# Revit family: QF_BPRO_TAW 10 GN_574240
name_source: partatom
category: Sonderausstattung
revit_build: Autodesk Revit 2018 (Build: 20190510_1515(x64)
units: mm (PartAtom-declared; Revit-internal decimal feet)

## family parameters
Arbeitsebenenbasiert = Nein
Beim Laden mit Abzugskörper schneiden = Nein
Bemaßung runder Anschluss = Durchmesser verwenden
Gemeinsam genutzt = Nein
Immer vertikal = Ja
OmniClass-Nummer = 23.40.40.00
OmniClass-Titel = Food Service Equipment and Furnishings
Raumberechnungspunkt = Nein
Teiletyp = Normal

## types (1)
- TAW 10 GN
    Artikel Nummer = 574240
    Barcode = 0
    Beschreibung = Tablett-Abrümwagen, 1-teilig, beidseitig beschickbar
    Beschreibung durch Hersteller analog Leistungsverzeichniskurztext = Tablett-Abräumwagen, TAW 10 GN


Abmessungen

Länge:				     468 mm
Breite:			     673 mm  
Höhe:			   1550 mm
Höhe inkl. Wagendach (optional):   1586 mm



Ausführung

Der Tablett-Abräumwagen ist einteilig und komplett in CNS 18/10, Werkstoff-Nr. 1.4301 ausgeführt. Die Rahmenkonstruktion besteht aus stabilem Vierkantrohr (25x25 mm und 40x20 mm) und ist komplett verschweißt.
Die Tablettauflagen aus Rundmaterial Ø 6 mm sind als Gestelle ausgeführt, die innerhalb des Rahmens eingehängt und sicher verschraubt sind. Dadurch sind die Auflagegestelle bei Bedarf komplett entnehmbar. Durch die schräg angeschweißten Bügel sind die Tablettauflagen mit integrierter, beidseitiger Durchschubsicherung ausgeführt.
Der Tablett-Abräumwagen kann von beiden Seiten beschickt werden und hat eine Kapazität von 10 Tabletts im GN-Format (530x325 mm). Der Auflagenabstand beträgt 125 mm.
Der Wagen ist fahr¬bar mittels rostfreien Kunststoffrollen gemäß DIN 18867, Teil 8 (4 Lenkrollen, davon 2 mit Feststeller, Rollendurchmesser 125 mm). Runde Wandabweiser aus Kunststoff (Polyamid) an allen vier Ecken schützen vor Beschädigungen.


Zubehör/ Optionen

•	Verkleidung 2-seitig aus Feinblech, doppelseitig elektrolytisch verzinkt, pulverbeschichtet in verschiedenen Farben, zum Einhängen an den Tablett-Abräumwagen. Zur Reinigung einfach und ohne Werkzeug abnehmbar.
•	Verkleidung 2-seitig aus Edelstahl, zum Einhängen an den Tablett-Abräumwagen. Zur Reinigung einfach und ohne Werkzeug abnehmbar.
•	Verkleidung 3-seitig aus Feinblech, doppelseitig elektrolytisch verzinkt, pulverbeschichtet in verschiedenen Farben, zum Einhängen an den Tablett-Abräumwagen. Zur Reinigung einfach und ohne Werkzeug abnehmbar.
•	Verkleidung 3-seitig aus Edelstahl, zum Einhängen an den Tablett-Abräumwagen. Zur Reinigung einfach und ohne Werkzeug abnehmbar.
•	Tür aus Feinblech, zweiwandig für mehr Stabilität, doppelseitig elektrolytisch verzinkt, pulverbeschichtet in verschiedenen Farben. Wahlweise geschlossen oder mit Glaseinsatz aus Einscheiben-Sicherheitsglas (ESG) erhältlich.
•	Tür aus Edelstahl. Wahlweise geschlossen oder mit Glaseinsatz aus Einscheiben-Sicherheitsglas (ESG) erhältlich.
•	Wagendach aus Edelstahl inkl. umlaufender Galerie. Zum Aufsetzen auf den Tablett-Abräumwagen. Zur Reinigung einfach und ohne Werkzeug abnehmbar. Die maximale Flächenlast beträgt 20 kg.
•	Boden aus Edelstahl zum Einlegen in die Rahmenkonstruktion. Zur Reinigung einfach und ohne Werkzeug abnehmbar.
•	Zusätzliche Durchschubsicherung aus Edelstahl
•	Schiebegriff stirnseitig
•	Rollensatz stahlverzinkt


Technische Daten

Werkstoff:		Chromnickelstahl 18/10, Polyamid (PA)	
Gewicht:	ca. 21 kg
Max. Tragfähigkeit Wagen:	150 kg
Max. Tragfähigkeit/ 
Auflagenpaar:	4,5 kg
Anzahl der Auflagenpaare:	10
Kapazität:	 		10 Gastronorm-Tabletts, 		530x325 mm
Auflagenabstand:	125 mm
	

Besonderheit

•	Tablettauflagen mit integrierter, beidseitiger Durchschubsicherung
•	Tablettauflagegestelle komplett entnehmbar
•	Optionale Verkleidung (2-, oder 3-seitig) zum Einhängen an den TAW. Dadurch zur Reinigung einfach abnehmbar.
•	Anbauteile wie Verkleidung, Türen, Dach und Boden jederzeit nachrüstbar.



Fabrikat

Hersteller:			B.PRO
Modell:	TAW 10 GN
Best.Nr.	574 240
    Beschreibung durch Hersteller analog Leistungsverzeichnislangtext = Tablett-Abräumwagen, TAW 10 GN


Abmessungen

Länge:				     468 mm
Breite:			     673 mm  
Höhe:			   1550 mm
Höhe inkl. Wagendach (optional):   1586 mm



Ausführung

Der Tablett-Abräumwagen ist einteilig und komplett in CNS 18/10, Werkstoff-Nr. 1.4301 ausgeführt. Die Rahmenkonstruktion besteht aus stabilem Vierkantrohr (25x25 mm und 40x20 mm) und ist komplett verschweißt.
Die Tablettauflagen aus Rundmaterial Ø 6 mm sind als Gestelle ausgeführt, die innerhalb des Rahmens eingehängt und sicher verschraubt sind. Dadurch sind die Auflagegestelle bei Bedarf komplett entnehmbar. Durch die schräg angeschweißten Bügel sind die Tablettauflagen mit integrierter, beidseitiger Durchschubsicherung ausgeführt.
Der Tablett-Abräumwagen kann von beiden Seiten beschickt werden und hat eine Kapazität von 10 Tabletts im GN-Format (530x325 mm). Der Auflagenabstand beträgt 125 mm.
Der Wagen ist fahr¬bar mittels rostfreien Kunststoffrollen gemäß DIN 18867, Teil 8 (4 Lenkrollen, davon 2 mit Feststeller, Rollendurchmesser 125 mm). Runde Wandabweiser aus Kunststoff (Polyamid) an allen vier Ecken schützen vor Beschädigungen.


Zubehör/ Optionen

•	Verkleidung 2-seitig aus Feinblech, doppelseitig elektrolytisch verzinkt, pulverbeschichtet in verschiedenen Farben, zum Einhängen an den Tablett-Abräumwagen. Zur Reinigung einfach und ohne Werkzeug abnehmbar.
•	Verkleidung 2-seitig aus Edelstahl, zum Einhängen an den Tablett-Abräumwagen. Zur Reinigung einfach und ohne Werkzeug abnehmbar.
•	Verkleidung 3-seitig aus Feinblech, doppelseitig elektrolytisch verzinkt, pulverbeschichtet in verschiedenen Farben, zum Einhängen an den Tablett-Abräumwagen. Zur Reinigung einfach und ohne Werkzeug abnehmbar.
•	Verkleidung 3-seitig aus Edelstahl, zum Einhängen an den Tablett-Abräumwagen. Zur Reinigung einfach und ohne Werkzeug abnehmbar.
•	Tür aus Feinblech, zweiwandig für mehr Stabilität, doppelseitig elektrolytisch verzinkt, pulverbeschichtet in verschiedenen Farben. Wahlweise geschlossen oder mit Glaseinsatz aus Einscheiben-Sicherheitsglas (ESG) erhältlich.
•	Tür aus Edelstahl. Wahlweise geschlossen oder mit Glaseinsatz aus Einscheiben-Sicherheitsglas (ESG) erhältlich.
•	Wagendach aus Edelstahl inkl. umlaufender Galerie. Zum Aufsetzen auf den Tablett-Abräumwagen. Zur Reinigung einfach und ohne Werkzeug abnehmbar. Die maximale Flächenlast beträgt 20 kg.
•	Boden aus Edelstahl zum Einlegen in die Rahmenkonstruktion. Zur Reinigung einfach und ohne Werkzeug abnehmbar.
•	Zusätzliche Durchschubsicherung aus Edelstahl
•	Schiebegriff stirnseitig
•	Rollensatz stahlverzinkt


Technische Daten

Werkstoff:		Chromnickelstahl 18/10, Polyamid (PA)	
Gewicht:	ca. 21 kg
Max. Tragfähigkeit Wagen:	150 kg
Max. Tragfähigkeit/ 
Auflagenpaar:	4,5 kg
Anzahl der Auflagenpaare:	10
Kapazität:	 		10 Gastronorm-Tabletts, 		530x325 mm
Auflagenabstand:	125 mm
	

Besonderheit

•	Tablettauflagen mit integrierter, beidseitiger Durchschubsicherung
•	Tablettauflagegestelle komplett entnehmbar
•	Optionale Verkleidung (2-, oder 3-seitig) zum Einhängen an den TAW. Dadurch zur Reinigung einfach abnehmbar.
•	Anbauteile wie Verkleidung, Türen, Dach und Boden jederzeit nachrüstbar.



Fabrikat

Hersteller:			B.PRO
Modell:	TAW 10 GN
Best.Nr.	574 240
    Ersteller = 123D World, APV-Digital
    Gerätegewicht Netto = 21.00 kg
    Großküchengerätezuordnung = Ja
    Hersteller = B.PRO GmbH
    Höhe = 1550 mm  [stored 5.0853 ft]
    Internetadresse Gerätehersteller = https://www.bpro-solutions.com
    Internetadresse für Ersatzteilliste = https://www.bpro-solutions.com
    Internetadresse für kritische Ersatzteilliste = https://www.bpro-solutions.com
    Kosten = 532 $
    Länge Gerätebreite = 468 mm  [stored 1.53543 ft]
    Modell = TAW 10 GN
    Punktlast = 150
    Tiefe = 673 mm  [stored 2.20801 ft]
    Typenkommentare = Tablett-Abrümwagen, 1-teilig, beidseitig beschickbar
    URL = https://www.bpro-solutions.com
    Zubehör = Nein

note: [stored X ft] marks values corroborated as IEEE doubles in the binary element streams (Revit-internal decimal feet)
